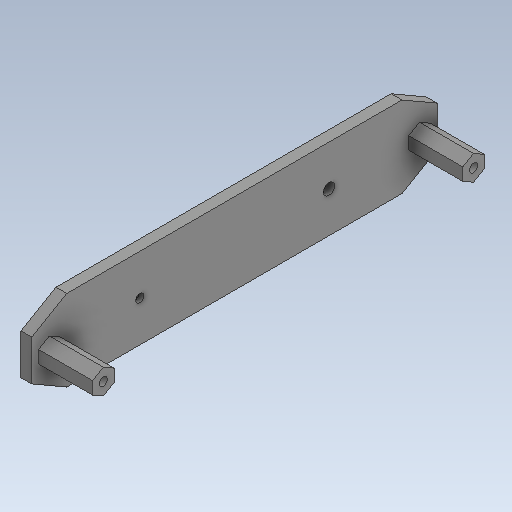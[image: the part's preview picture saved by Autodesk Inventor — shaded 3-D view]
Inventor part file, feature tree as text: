
AUTODESK INVENTOR PART (.ipt)
format: ipt  version: 2020 (Build 240168000, 168)  size: 236,032 bytes
history: native  units: in
note: dims shown in document units (in); Inventor stores cm internally (conversion verified against a paired STEP export)
features: extrude x7, sketch x7, plane x1
ambient origin geometry x8: Origin, YZ Plane, XZ Plane, XY Plane, X Axis, Y Axis, Z Axis, Center Point
bodies: Solid1 (feature_tree)
feature tree (15):
  extrude  "Extrusion1"  Depth=5.9055in
  extrude  "Extrusion3"  TaperAngle=0.0deg  [1 undecoded]
  extrude  "Extrusion4"  Depth=0.7874in
  plane  "Work Plane1"
  extrude  "Extrusion5"  Depth=0.122in
  extrude  "Extrusion6"  Depth=0.2402in
  extrude  "Extrusion7"  [1 undecoded]
  extrude  "Extrusion8"  Depth=0.0866in TaperAngle=0.0deg
  sketch  "Sketch1"  dims[d0=1.1811in d1=5.9055in]
  sketch  "Sketch2"  dims[d2=0.1575in d3=0.0in]
  sketch  "Sketch3"  dims[d8=0.315in d9=0.7874in]
  sketch  "Sketch4"  dims[d10=0.0in d12=0.122in]
  sketch  "Sketch5"  dims[d13=0.0in d14=0.0in d15=0.2402in]
  sketch  "Sketch8"  dims[d16=0.0866in d17=-0.2233in]
  sketch  "Sketch9"  dims[d18=-0.3937in d19=0.0866in d20=0.0in d26=1.5748in d27=0.1654in d28=0.122in d29=1.5748in d30=0.0in d31=0.0in d32=0.2402in d33=0.0866in d34=-0.2233in]
note: 2 required parameter values undecoded (feature->parameter linkage not recoverable at this tier; creation-order binding heuristic only, values carry confidence <= 0.55)
